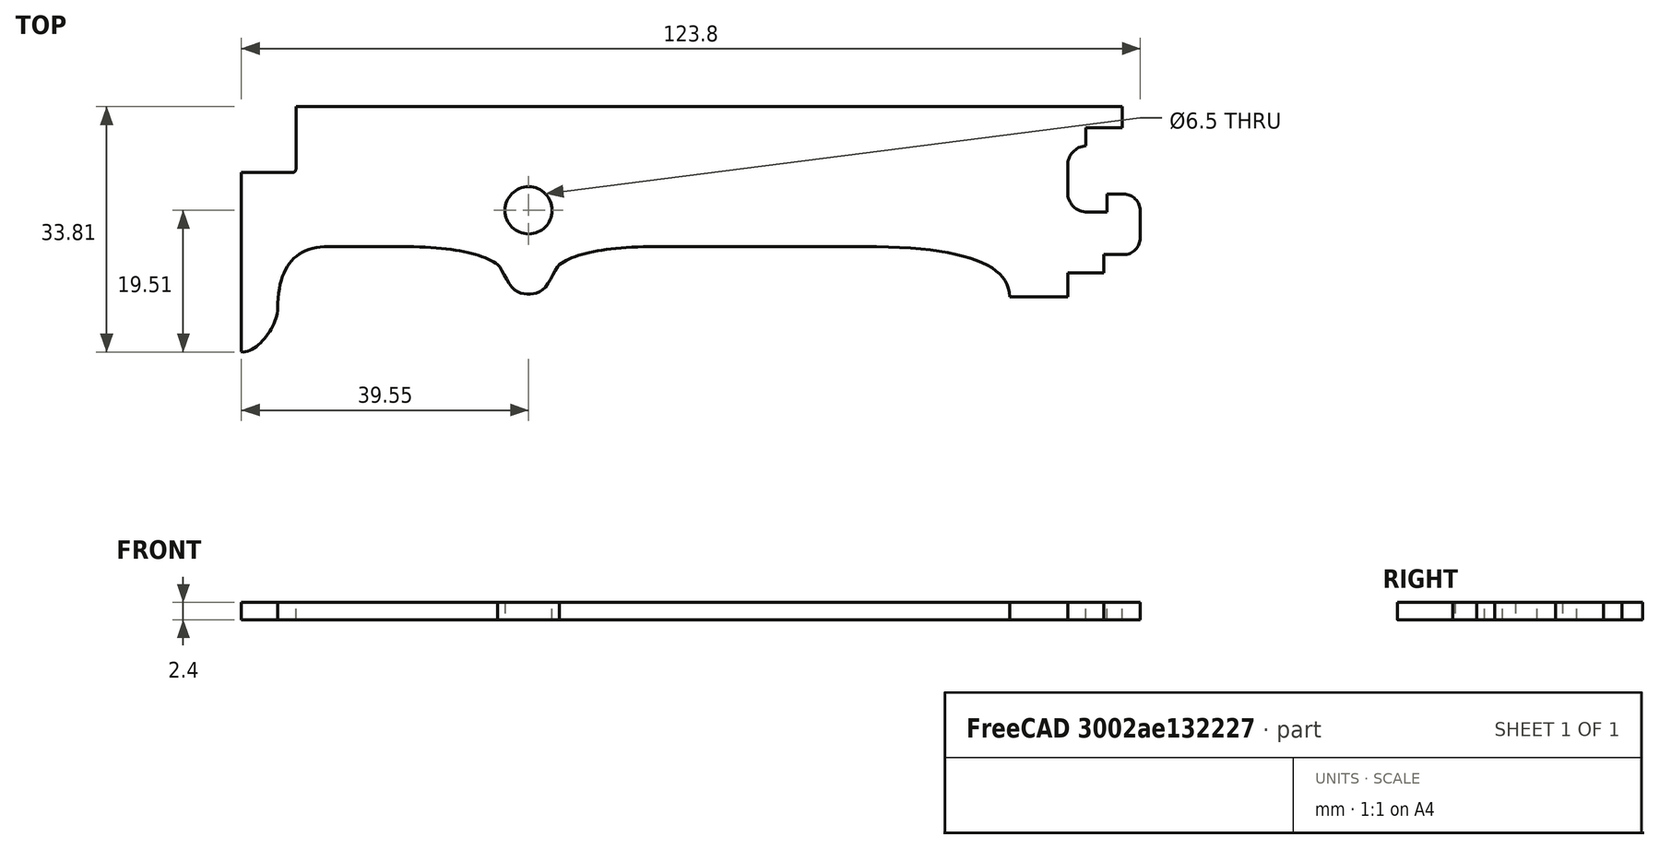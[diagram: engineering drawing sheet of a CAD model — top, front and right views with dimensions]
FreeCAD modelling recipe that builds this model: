
FCSTD DOCUMENT  (FreeCAD 0.19R0.19.2)
Label: v0_12
License: All rights reserved
LicenseURL: http://en.wikipedia.org/wiki/All_rights_reserved
objects: Sketcher::SketchObject×2, Part::Extrusion×1
note: 3 computed .brp shape members not serialized (recipe doc carries the construction recipe); baked Part::Feature solids carry a one-line shape summary decoded from their .brp

FEATURE [Sketcher::SketchObject] Sketch
  FullyConstrained = true
  sketch-geometry (69):
    g0: ArcOfCircle CenterX=-20 CenterY=-14.35 CenterZ=0 NormalX=0 NormalY=0 NormalZ=1 AngleXU=0 Radius=2.3 StartAngle=8e-16 EndAngle=1.5708
    g1: ArcOfCircle CenterX=-20 CenterY=-18.1 CenterZ=0 NormalX=0 NormalY=0 NormalZ=1 AngleXU=0 Radius=2.3 StartAngle=4.71239 EndAngle=6.28319
    g2: LineSegment StartX=-20 StartY=-20.4 StartZ=0 EndX=-22.7 EndY=-20.4 EndZ=0
    g3: LineSegment StartX=-22.7 StartY=-22.9 StartZ=0 EndX=-22.7 EndY=-20.4 EndZ=0
    g4: LineSegment StartX=-17.7 StartY=-14.35 StartZ=0 EndX=-17.7 EndY=-18.1 EndZ=0
    g5: LineSegment StartX=-25.2 StartY=-5.40742 StartZ=0 EndX=-25.2 EndY=-2.9 EndZ=0
    g6: LineSegment StartX=-25.2 StartY=-2.9 StartZ=0 EndX=-20.2 EndY=-2.9 EndZ=0
    g7: LineSegment StartX=-20.2 StartY=-2.9 StartZ=0 EndX=-20.2 EndY=0 EndZ=0
    g8: ArcOfCircle CenterX=-25 CenterY=-8.1 CenterZ=0 NormalX=0 NormalY=0 NormalZ=1 AngleXU=0 Radius=2.7 StartAngle=1.64494 EndAngle=3.14159
    g9: ArcOfCircle CenterX=-25 CenterY=-11.85 CenterZ=0 NormalX=0 NormalY=0 NormalZ=1 AngleXU=0 Radius=2.7 StartAngle=3.14159 EndAngle=4.71239
    g10: LineSegment StartX=-27.7 StartY=-8.1 StartZ=0 EndX=-27.7 EndY=-11.85 EndZ=0
    g11: LineSegment StartX=-25 StartY=-14.55 StartZ=0 EndX=-22.3 EndY=-14.55 EndZ=0
    g12: LineSegment StartX=-22.3 StartY=-12.05 StartZ=0 EndX=-22.3 EndY=-14.55 EndZ=0
    g13: LineSegment StartX=-22.3 StartY=-12.05 StartZ=0 EndX=-20 EndY=-12.05 EndZ=0
    g14: LineSegment StartX=-27.7 StartY=-22.9 StartZ=0 EndX=-22.7 EndY=-22.9 EndZ=0
    g15: LineSegment StartX=-27.7 StartY=-22.9 StartZ=0 EndX=-27.7 EndY=-26.2 EndZ=0
    g16: Circle CenterX=-101.95 CenterY=-14.3 CenterZ=0 NormalX=0 NormalY=0 NormalZ=1 AngleXU=0 Radius=3.25
    g17: LineSegment StartX=-134 StartY=0 StartZ=0 EndX=-20.2 EndY=0 EndZ=0
    g18: LineSegment StartX=-134 StartY=2.68e-14 StartZ=0 EndX=-134 EndY=-8.6 EndZ=0
    g19: LineSegment StartX=-134.5 StartY=-9.1 StartZ=0 EndX=-141.5 EndY=-9.1 EndZ=0
    g20: ArcOfCircle CenterX=-134.5 CenterY=-8.6 CenterZ=0 NormalX=0 NormalY=0 NormalZ=1 AngleXU=0 Radius=0.5 StartAngle=4.71239 EndAngle=6.28319
    g21: Circle CenterX=-97.7 CenterY=-21.8 CenterZ=0 NormalX=0 NormalY=0 NormalZ=1 AngleXU=0 Radius=1
    g22: Circle CenterX=-94.45 CenterY=-19.3 CenterZ=0 NormalX=0 NormalY=0 NormalZ=1 AngleXU=0 Radius=1
    g23: Circle CenterX=-84.45 CenterY=-19.3 CenterZ=0 NormalX=0 NormalY=0 NormalZ=1 AngleXU=0 Radius=1
    g24: BSplineCurve PolesCount=3 KnotsCount=2 Degree=2 IsPeriodic=0
    g25: GeomPoint X=-97.7 Y=-21.8 Z=0
    g26: GeomPoint X=-84.45 Y=-19.3 Z=0
    g27: Circle CenterX=-106.2 CenterY=-21.8 CenterZ=0 NormalX=0 NormalY=0 NormalZ=1 AngleXU=0 Radius=1
    g28: Circle CenterX=-109.45 CenterY=-19.3 CenterZ=0 NormalX=0 NormalY=0 NormalZ=1 AngleXU=0 Radius=1
    g29: Circle CenterX=-119.45 CenterY=-19.3 CenterZ=0 NormalX=0 NormalY=0 NormalZ=1 AngleXU=0 Radius=1
    g30: BSplineCurve PolesCount=3 KnotsCount=2 Degree=2 IsPeriodic=0
    g31: GeomPoint X=-106.2 Y=-21.8 Z=0
    g32: GeomPoint X=-119.45 Y=-19.3 Z=0
    g33: LineSegment StartX=-141.5 StartY=-9.1 StartZ=0 EndX=-141.5 EndY=-33.8 EndZ=0
    g34-g37: Circle x4 (B-spline internal-alignment scaffolding for g38; pole/knot coordinates omitted)
    g38: BSplineCurve PolesCount=4 KnotsCount=2 Degree=3 IsPeriodic=0
    g39: GeomPoint X=-141.5 Y=-33.8 Z=0
    g40: GeomPoint X=-136.5 Y=-27.8 Z=0
    g41: Circle CenterX=-136.5 CenterY=-27.8 CenterZ=0 NormalX=0 NormalY=0 NormalZ=1 AngleXU=0 Radius=1
    g42: Circle CenterX=-136.5 CenterY=-19.3 CenterZ=0 NormalX=0 NormalY=0 NormalZ=1 AngleXU=0 Radius=1
    g43: Circle CenterX=-129.5 CenterY=-19.3 CenterZ=0 NormalX=0 NormalY=0 NormalZ=1 AngleXU=0 Radius=1
    g44: BSplineCurve PolesCount=3 KnotsCount=2 Degree=2 IsPeriodic=0
    g45: GeomPoint X=-136.5 Y=-27.8 Z=0
    g46: GeomPoint X=-129.5 Y=-19.3 Z=0
    g47: LineSegment StartX=-129.5 StartY=-19.3 StartZ=0 EndX=-119.45 EndY=-19.3 EndZ=0
    g48: LineSegment StartX=-35.7 StartY=-26.2 StartZ=0 EndX=-27.7 EndY=-26.2 EndZ=0
    g49: Circle CenterX=-35.7 CenterY=-26.2 CenterZ=0 NormalX=0 NormalY=0 NormalZ=1 AngleXU=0 Radius=1
    g50: Circle CenterX=-35.7 CenterY=-19.3 CenterZ=0 NormalX=0 NormalY=0 NormalZ=1 AngleXU=0 Radius=1
    g51: Circle CenterX=-55.7 CenterY=-19.3 CenterZ=0 NormalX=0 NormalY=0 NormalZ=1 AngleXU=0 Radius=1
    g52: BSplineCurve PolesCount=3 KnotsCount=2 Degree=2 IsPeriodic=0
    g53: GeomPoint X=-35.7 Y=-26.2 Z=0
    g54: GeomPoint X=-55.7 Y=-19.3 Z=0
    g55: LineSegment StartX=-84.45 StartY=-19.3 StartZ=0 EndX=-55.7 EndY=-19.3 EndZ=0
    g56-g62: Circle x7 (B-spline internal-alignment scaffolding for g63; pole/knot coordinates omitted)
    g63: BSplineCurve PolesCount=7 KnotsCount=5 Degree=3 IsPeriodic=0
    g64-g68: GeomPoint x5 (B-spline internal-alignment scaffolding for g63; pole/knot coordinates omitted)
  constraints (111):
    c: Block(g1)
    c: Block(g0)
    c: Coincident(g2,g1)
    c: Horizontal(g2)
    c: Vertical(g3)
    c: Coincident(g3,g2)
    c: Coincident(g4,g0)
    c: Coincident(g4,g1)
    c: Vertical(g4)
    c: Vertical(g5)
    c: Block(g5)
    c: Coincident(g6,g5)
    c: Horizontal(g6)
    c: Vertical(g7)
    c: Block(g7)
    c: Block(g6)
    c: Coincident(g8,g5)
    c: Block(g9)
    c: Coincident(g10,g8)
    c: Coincident(g10,g9)
    c: Vertical(g10)
    c: Block(g10)
    c: Coincident(g11,g9)
    c: Horizontal(g11)
    c: Vertical(g12)
    c: Coincident(g12,g11)
    c: Block(g12)
    c: Coincident(g13,g0)
    c: Horizontal(g13)
    c: Block(g13)
    c: Coincident(g14,g3)
    c: Horizontal(g14)
    c: Block(g14)
    c: Coincident(g15,g14)
    c: Vertical(g15)
    c: Block(g16)
    c: Coincident(g17,g7)
    c: Horizontal(g17)
    c: Vertical(g18)
    c: Distance(g18) = 8.6
    c: Horizontal(g19)
    c: Distance(g19) = 7
    c: Coincident(g20,g18)
    c: Coincident(g20,g19)
    c: Block(g20)
    c: Block(g17)
    c: Weight(g21) = 1
    c: Equal(g21,g22)
    c: Equal(g21,g23)
    c: InternalAlignment(g21,g24)
    c: InternalAlignment(g22,g24)
    c: InternalAlignment(g23,g24)
    c: InternalAlignment(g25,g24)
    c: InternalAlignment(g26,g24)
    c: Weight(g27) = 1
    c: Equal(g27,g28)
    c: Equal(g27,g29)
    c: InternalAlignment(g27,g30)
    c: InternalAlignment(g28,g30)
    c: InternalAlignment(g29,g30)
    c: InternalAlignment(g31,g30)
    c: InternalAlignment(g32,g30)
    c: Block(g30)
    c: Block(g24)
    c: Coincident(g33,g19)
    c: Vertical(g33)
    c: Block(g33)
    c: Coincident(g38,g33)
    c: Weight(g34) = 1
    c: Equal(g34,g35)
    c: Equal(g34,g36)
    c: Equal(g34,g37)
    c: InternalAlignment(g34-g37 -> g38) x4
    c: InternalAlignment(g39,g38)
    c: InternalAlignment(g40,g38)
    c: Weight(g41) = 1
    c: Equal(g41,g42)
    c: Equal(g41,g43)
    c: InternalAlignment(g41,g44)
    c: InternalAlignment(g42,g44)
    c: InternalAlignment(g43,g44)
    c: InternalAlignment(g45,g44)
    c: InternalAlignment(g46,g44)
    c: Block(g38)
    c: Block(g44)
    c: Coincident(g47,g44)
    c: Coincident(g47,g30)
    c: Horizontal(g47)
    c: Horizontal(g48)
    c: Distance(g48) = 8
    c: Block(g48)
    c: Block(g15)
    c: Block(g8)
    c: Coincident(g52,g48)
    c: Weight(g49) = 1
    c: Equal(g49,g50)
    c: Equal(g49,g51)
    c: InternalAlignment(g49,g52)
    c: InternalAlignment(g50,g52)
    c: InternalAlignment(g51,g52)
    c: InternalAlignment(g53,g52)
    c: InternalAlignment(g54,g52)
    c: Block(g52)
    c: Coincident(g55,g24)
    c: Coincident(g55,g52)
    c: Horizontal(g55)
    c: Weight(g56) = 1
    c: Equal(g56, g57-g62) x6
    c: InternalAlignment(g56-g62 -> g63) x7
    c: InternalAlignment(g64-g68 -> g63) x5
    c: Block(g63)
FEATURE [Part::Extrusion] Extrude
  Base = -> Sketch
  Dir = (0,0,1)
  DirMode = 2
  FaceMakerClass = Part::FaceMakerBullseye
  LengthFwd = 2.4
  LengthRev = 0
  Solid = true
  Symmetric = false
FEATURE [Sketcher::SketchObject] Sketch001
  FullyConstrained = true
  sketch-geometry (74):
    g0: ArcOfCircle CenterX=-20 CenterY=-14.35 CenterZ=0 NormalX=0 NormalY=0 NormalZ=1 AngleXU=0 Radius=2.3 StartAngle=8e-16 EndAngle=1.5708
    g1: ArcOfCircle CenterX=-20 CenterY=-18.1 CenterZ=0 NormalX=0 NormalY=0 NormalZ=1 AngleXU=0 Radius=2.3 StartAngle=4.71239 EndAngle=6.28319
    g2: LineSegment StartX=-20 StartY=-20.4 StartZ=0 EndX=-22.7 EndY=-20.4 EndZ=0
    g3: LineSegment StartX=-22.7 StartY=-22.9 StartZ=0 EndX=-22.7 EndY=-20.4 EndZ=0
    g4: LineSegment StartX=-17.7 StartY=-14.35 StartZ=0 EndX=-17.7 EndY=-18.1 EndZ=0
    g5: LineSegment StartX=-25.2 StartY=-5.40742 StartZ=0 EndX=-25.2 EndY=-2.9 EndZ=0
    g6: LineSegment StartX=-25.2 StartY=-2.9 StartZ=0 EndX=-20.2 EndY=-2.9 EndZ=0
    g7: LineSegment StartX=-20.2 StartY=-2.9 StartZ=0 EndX=-20.2 EndY=0 EndZ=0
    g8: ArcOfCircle CenterX=-25 CenterY=-8.1 CenterZ=0 NormalX=0 NormalY=0 NormalZ=1 AngleXU=0 Radius=2.7 StartAngle=1.64494 EndAngle=3.14159
    g9: ArcOfCircle CenterX=-25 CenterY=-11.85 CenterZ=0 NormalX=0 NormalY=0 NormalZ=1 AngleXU=0 Radius=2.7 StartAngle=3.14159 EndAngle=4.71239
    g10: LineSegment StartX=-27.7 StartY=-8.1 StartZ=0 EndX=-27.7 EndY=-11.85 EndZ=0
    g11: LineSegment StartX=-25 StartY=-14.55 StartZ=0 EndX=-22.3 EndY=-14.55 EndZ=0
    g12: LineSegment StartX=-22.3 StartY=-12.05 StartZ=0 EndX=-22.3 EndY=-14.55 EndZ=0
    g13: LineSegment StartX=-22.3 StartY=-12.05 StartZ=0 EndX=-20 EndY=-12.05 EndZ=0
    g14: LineSegment StartX=-27.7 StartY=-22.9 StartZ=0 EndX=-22.7 EndY=-22.9 EndZ=0
    g15: LineSegment StartX=-27.7 StartY=-22.9 StartZ=0 EndX=-27.7 EndY=-26.2 EndZ=0
    g16: Circle CenterX=-101.95 CenterY=-14.3 CenterZ=0 NormalX=0 NormalY=0 NormalZ=1 AngleXU=0 Radius=3.25
    g17: LineSegment StartX=-134 StartY=0 StartZ=0 EndX=-134 EndY=-8.6 EndZ=0
    g18: LineSegment StartX=-134.5 StartY=-9.1 StartZ=0 EndX=-141.5 EndY=-9.1 EndZ=0
    g19: ArcOfCircle CenterX=-134.5 CenterY=-8.6 CenterZ=0 NormalX=0 NormalY=0 NormalZ=1 AngleXU=0 Radius=0.5 StartAngle=4.71239 EndAngle=6.28319
    g20: Circle CenterX=-97.7 CenterY=-21.8 CenterZ=0 NormalX=0 NormalY=0 NormalZ=1 AngleXU=0 Radius=1
    g21: Circle CenterX=-94.45 CenterY=-19.3 CenterZ=0 NormalX=0 NormalY=0 NormalZ=1 AngleXU=0 Radius=1
    g22: Circle CenterX=-84.45 CenterY=-19.3 CenterZ=0 NormalX=0 NormalY=0 NormalZ=1 AngleXU=0 Radius=1
    g23: BSplineCurve PolesCount=3 KnotsCount=2 Degree=2 IsPeriodic=0
    g24: GeomPoint X=-97.7 Y=-21.8 Z=0
    g25: GeomPoint X=-84.45 Y=-19.3 Z=0
    g26: Circle CenterX=-106.2 CenterY=-21.8 CenterZ=0 NormalX=0 NormalY=0 NormalZ=1 AngleXU=0 Radius=1
    g27: Circle CenterX=-109.45 CenterY=-19.3 CenterZ=0 NormalX=0 NormalY=0 NormalZ=1 AngleXU=0 Radius=1
    g28: Circle CenterX=-119.45 CenterY=-19.3 CenterZ=0 NormalX=0 NormalY=0 NormalZ=1 AngleXU=0 Radius=1
    g29: BSplineCurve PolesCount=3 KnotsCount=2 Degree=2 IsPeriodic=0
    g30: GeomPoint X=-106.2 Y=-21.8 Z=0
    g31: GeomPoint X=-119.45 Y=-19.3 Z=0
    g32: LineSegment StartX=-141.5 StartY=-9.1 StartZ=0 EndX=-141.5 EndY=-33.8 EndZ=0
    g33-g36: Circle x4 (B-spline internal-alignment scaffolding for g37; pole/knot coordinates omitted)
    g37: BSplineCurve PolesCount=4 KnotsCount=2 Degree=3 IsPeriodic=0
    g38: GeomPoint X=-141.5 Y=-33.8 Z=0
    g39: GeomPoint X=-136.5 Y=-27.8 Z=0
    g40: Circle CenterX=-136.5 CenterY=-27.8 CenterZ=0 NormalX=0 NormalY=0 NormalZ=1 AngleXU=0 Radius=1
    g41: Circle CenterX=-136.5 CenterY=-19.3 CenterZ=0 NormalX=0 NormalY=0 NormalZ=1 AngleXU=0 Radius=1
    g42: Circle CenterX=-129.5 CenterY=-19.3 CenterZ=0 NormalX=0 NormalY=0 NormalZ=1 AngleXU=0 Radius=1
    g43: BSplineCurve PolesCount=3 KnotsCount=2 Degree=2 IsPeriodic=0
    g44: GeomPoint X=-136.5 Y=-27.8 Z=0
    g45: GeomPoint X=-129.5 Y=-19.3 Z=0
    g46: LineSegment StartX=-129.5 StartY=-19.3 StartZ=0 EndX=-119.45 EndY=-19.3 EndZ=0
    g47: LineSegment StartX=-35.7 StartY=-26.2 StartZ=0 EndX=-27.7 EndY=-26.2 EndZ=0
    g48: Circle CenterX=-35.7 CenterY=-26.2 CenterZ=0 NormalX=0 NormalY=0 NormalZ=1 AngleXU=0 Radius=1
    g49: Circle CenterX=-35.7 CenterY=-19.3 CenterZ=0 NormalX=0 NormalY=0 NormalZ=1 AngleXU=0 Radius=1
    g50: Circle CenterX=-55.7 CenterY=-19.3 CenterZ=0 NormalX=0 NormalY=0 NormalZ=1 AngleXU=0 Radius=1
    g51: BSplineCurve PolesCount=3 KnotsCount=2 Degree=2 IsPeriodic=0
    g52: GeomPoint X=-35.7 Y=-26.2 Z=0
    g53: GeomPoint X=-55.7 Y=-19.3 Z=0
    g54: LineSegment StartX=-84.45 StartY=-19.3 StartZ=0 EndX=-55.7 EndY=-19.3 EndZ=0
    g55-g61: Circle x7 (B-spline internal-alignment scaffolding for g62; pole/knot coordinates omitted)
    g62: BSplineCurve PolesCount=7 KnotsCount=5 Degree=3 IsPeriodic=0
    g63-g67: GeomPoint x5 (B-spline internal-alignment scaffolding for g62; pole/knot coordinates omitted)
    g68: LineSegment StartX=-131 StartY=0 StartZ=0 EndX=-131 EndY=-3 EndZ=0
    g69: LineSegment StartX=-134 StartY=0 StartZ=0 EndX=-20.2 EndY=0 EndZ=0
    g70: LineSegment StartX=-131 StartY=-3 StartZ=0 EndX=-35.7 EndY=-3 EndZ=0
    g71: LineSegment StartX=-35.7 StartY=-3 StartZ=0 EndX=-35.7 EndY=-16.3 EndZ=0
    g72: LineSegment StartX=-35.7 StartY=-16.3 StartZ=0 EndX=-97.7 EndY=-16.3 EndZ=0
    g73: LineSegment StartX=-129.5 StartY=-16.3 StartZ=0 EndX=-106.2 EndY=-16.3 EndZ=0
  constraints (124):
    c: Block(g1)
    c: Block(g0)
    c: Coincident(g2,g1)
    c: Horizontal(g2)
    c: Vertical(g3)
    c: Coincident(g3,g2)
    c: Coincident(g4,g0)
    c: Coincident(g4,g1)
    c: Vertical(g4)
    c: Vertical(g5)
    c: Block(g5)
    c: Coincident(g6,g5)
    c: Horizontal(g6)
    c: Vertical(g7)
    c: Block(g7)
    c: Block(g6)
    c: Coincident(g8,g5)
    c: Block(g9)
    c: Coincident(g10,g8)
    c: Coincident(g10,g9)
    c: Vertical(g10)
    c: Block(g10)
    c: Coincident(g11,g9)
    c: Horizontal(g11)
    c: Vertical(g12)
    c: Coincident(g12,g11)
    c: Block(g12)
    c: Coincident(g13,g0)
    c: Horizontal(g13)
    c: Block(g13)
    c: Coincident(g14,g3)
    c: Horizontal(g14)
    c: Block(g14)
    c: Coincident(g15,g14)
    c: Vertical(g15)
    c: Block(g16)
    c: Vertical(g17)
    c: Distance(g17) = 8.6
    c: Horizontal(g18)
    c: Distance(g18) = 7
    c: Coincident(g19,g17)
    c: Coincident(g19,g18)
    c: Block(g19)
    c: Weight(g20) = 1
    c: Equal(g20,g21)
    c: Equal(g20,g22)
    c: InternalAlignment(g20,g23)
    c: InternalAlignment(g21,g23)
    c: InternalAlignment(g22,g23)
    c: InternalAlignment(g24,g23)
    c: InternalAlignment(g25,g23)
    c: Weight(g26) = 1
    c: Equal(g26,g27)
    c: Equal(g26,g28)
    c: InternalAlignment(g26,g29)
    c: InternalAlignment(g27,g29)
    c: InternalAlignment(g28,g29)
    c: InternalAlignment(g30,g29)
    c: InternalAlignment(g31,g29)
    c: Block(g29)
    c: Block(g23)
    c: Coincident(g32,g18)
    c: Vertical(g32)
    c: Block(g32)
    c: Coincident(g37,g32)
    c: Weight(g33) = 1
    c: Equal(g33,g34)
    c: Equal(g33,g35)
    c: Equal(g33,g36)
    c: InternalAlignment(g33-g36 -> g37) x4
    c: InternalAlignment(g38,g37)
    c: InternalAlignment(g39,g37)
    c: Weight(g40) = 1
    c: Equal(g40,g41)
    c: Equal(g40,g42)
    c: InternalAlignment(g40,g43)
    c: InternalAlignment(g41,g43)
    c: InternalAlignment(g42,g43)
    c: InternalAlignment(g44,g43)
    c: InternalAlignment(g45,g43)
    c: Block(g37)
    c: Block(g43)
    c: Coincident(g46,g43)
    c: Coincident(g46,g29)
    c: Horizontal(g46)
    c: Horizontal(g47)
    c: Distance(g47) = 8
    c: Block(g47)
    c: Block(g15)
    c: Block(g8)
    c: Coincident(g51,g47)
    c: Weight(g48) = 1
    c: Equal(g48,g49)
    c: Equal(g48,g50)
    c: InternalAlignment(g48,g51)
    c: InternalAlignment(g49,g51)
    c: InternalAlignment(g50,g51)
    c: InternalAlignment(g52,g51)
    c: InternalAlignment(g53,g51)
    c: Block(g51)
    c: Coincident(g54,g23)
    c: Coincident(g54,g51)
    c: Horizontal(g54)
    c: Weight(g55) = 1
    c: Equal(g55, g56-g61) x6
    c: InternalAlignment(g55-g61 -> g62) x7
    c: InternalAlignment(g63-g67 -> g62) x5
    c: Block(g62)
    c: Vertical(g68)
    c: Distance(g68) = 3
    c: Coincident(g69,g17)
    c: Coincident(g69,g7)
    c: Horizontal(g69)
    c: Coincident(g70,g68)
    c: Horizontal(g70)
    c: Block(g70)
    c: Coincident(g71,g70)
    c: Vertical(g71)
    c: Block(g71)
    c: Coincident(g72,g71)
    c: Horizontal(g72)
    c: Horizontal(g73)
    c: Block(g73)
    c: Block(g72)
